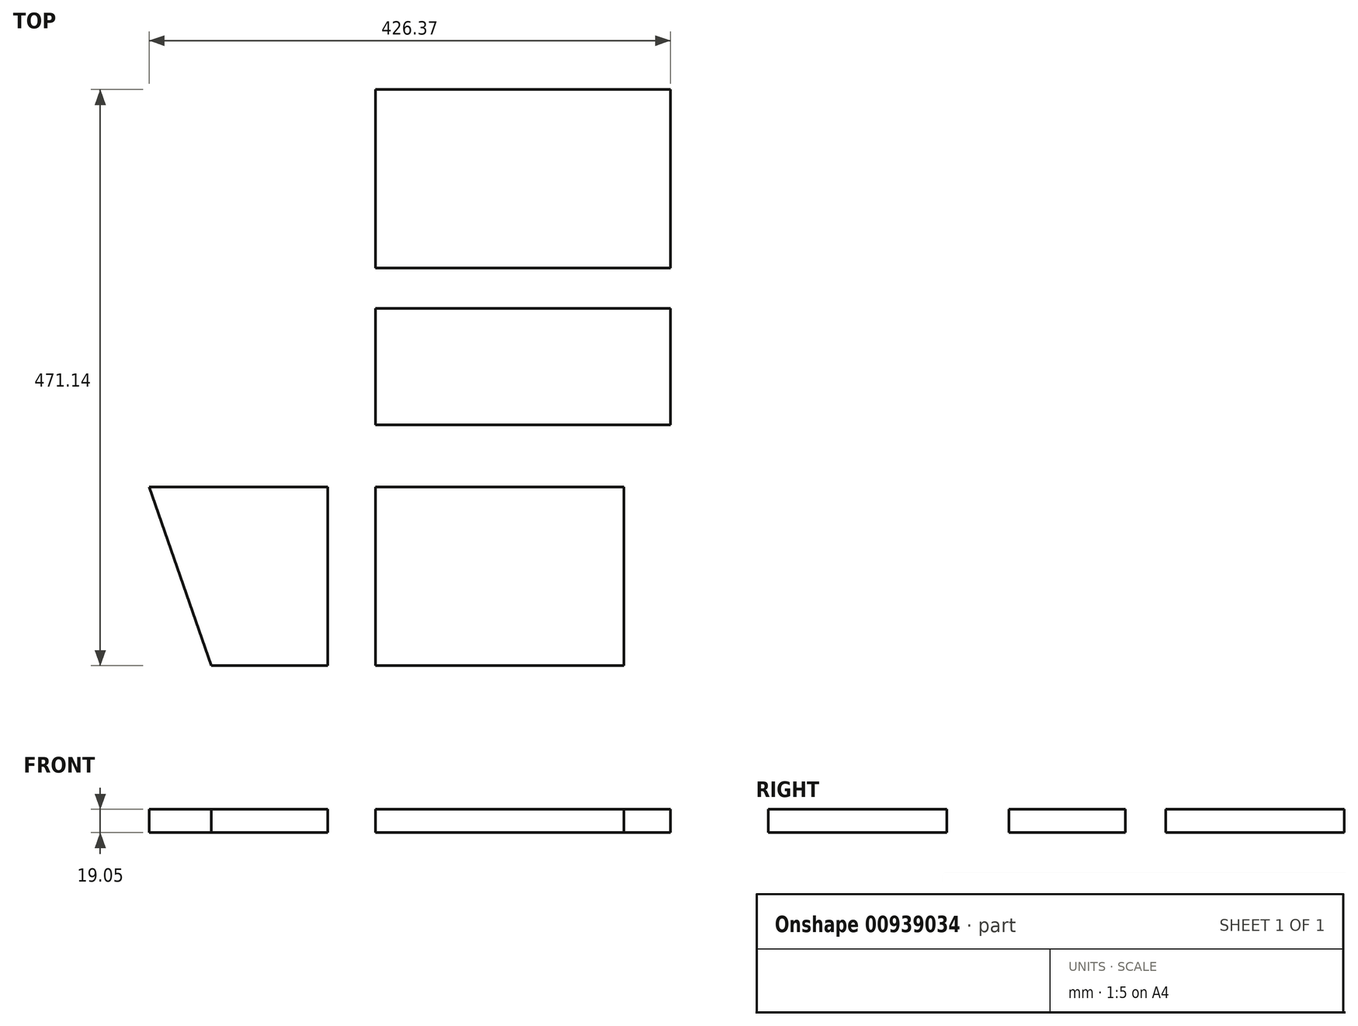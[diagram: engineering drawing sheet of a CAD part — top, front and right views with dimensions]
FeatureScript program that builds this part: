
annotation { "Feature Type Name" : "Feature", "Feature Type Description" : "" }
export const myFeature = defineFeature(function(context is Context, id is Id, definition is map)
    precondition{}
    {
        {
            var Q0;
            Q0=qCreatedBy(makeId("Front.planeOp"),FACE);
            var sketch = newSketch(context, id + "F0", { "sketchPlane" : qUnion([Q0])});
            skLineSegment(sketch, "E0.bottom", {"start": v(0, 0) * mm, "end": v(203.2, 0) * mm});
            skLineSegment(sketch, "E0.top", {"start": v(0, 19.05) * mm, "end": v(203.2, 19.05) * mm});
            skLineSegment(sketch, "E0.left", {"start": v(0, 0) * mm, "end": v(0, 19.05) * mm});
            skLineSegment(sketch, "E0.right", {"start": v(203.2, 0) * mm, "end": v(203.2, 19.05) * mm});
            skSolve(sketch);
        }
        {
            var Q0;
            Q0 = qSketchRegion(id + "F0", true);
            extrude(context, id + "F1", {"entities" : qUnion([Q0]), "depth" : 146.05 * mm, "offsetDistance" : 25.4 * mm});
        }
        {
            var Q0;
            Q0=qCreatedBy(makeId("Top.planeOp"),FACE);
            var sketch = newSketch(context, id + "F2", { "sketchPlane" : qUnion([Q0])});
            skLineSegment(sketch, "E1.bottom", {"start": v(0, 50.8) * mm, "end": v(241.3, 50.8) * mm});
            skLineSegment(sketch, "E1.top", {"start": v(0, 146.05) * mm, "end": v(241.3, 146.05) * mm});
            skLineSegment(sketch, "E1.left", {"start": v(0, 50.8) * mm, "end": v(0, 146.05) * mm});
            skLineSegment(sketch, "E1.right", {"start": v(241.3, 50.8) * mm, "end": v(241.3, 146.05) * mm});
            skSolve(sketch);
        }
        {
            var Q0;
            Q0 = qSketchRegion(id + "F2", true);
            extrude(context, id + "F3", {"entities" : qUnion([Q0]), "depth" : 19.05 * mm, "offsetDistance" : 25.4 * mm});
        }
        {
            var Q0;
            Q0=qCreatedBy(makeId("Top.planeOp"),FACE);
            var sketch = newSketch(context, id + "F4", { "sketchPlane" : qUnion([Q0])});
            skLineSegment(sketch, "E2.bottom", {"start": v(0, 179.04) * mm, "end": v(241.3, 179.04) * mm});
            skLineSegment(sketch, "E2.top", {"start": v(0, 325.09) * mm, "end": v(241.3, 325.09) * mm});
            skLineSegment(sketch, "E2.left", {"start": v(0, 179.04) * mm, "end": v(0, 325.09) * mm});
            skLineSegment(sketch, "E2.right", {"start": v(241.3, 179.04) * mm, "end": v(241.3, 325.09) * mm});
            skSolve(sketch);
        }
        {
            var Q0;
            Q0 = qSketchRegion(id + "F4", true);
            extrude(context, id + "F5", {"entities" : qUnion([Q0]), "depth" : 19.05 * mm, "offsetDistance" : 25.4 * mm});
        }
        {
            var Q0;
            Q0=qCreatedBy(makeId("Top.planeOp"),FACE);
            var sketch = newSketch(context, id + "F6", { "sketchPlane" : qUnion([Q0])});
            skLineSegment(sketch, "E3.bottom", {"start": v(-39.02, 0) * mm, "end": v(-185.07, 0) * mm});
            skLineSegment(sketch, "E3.top", {"start": v(-39.02, -146.05) * mm, "end": v(-185.07, -146.05) * mm});
            skLineSegment(sketch, "E3.left", {"start": v(-39.02, 0) * mm, "end": v(-39.02, -146.05) * mm});
            skLineSegment(sketch, "E3.right", {"start": v(-185.07, 0) * mm, "end": v(-185.07, -146.05) * mm});
            skSolve(sketch);
        }
        {
            var Q0;
            Q0 = qSketchRegion(id + "F6", true);
            extrude(context, id + "F7", {"entities" : qUnion([Q0]), "depth" : 19.05 * mm, "offsetDistance" : 25.4 * mm});
        }
        {
            var Q0;
            Q0=makeQuery(id+"F7.opExtrude","CAP_FACE",FACE,{"disambiguationData":[OSD([sQuery(id+"F6.wireOp",EDGE,"E3.bottom"),sQuery(id+"F6.wireOp",EDGE,"E3.top"),sQuery(id+"F6.wireOp",EDGE,"E3.left"),sQuery(id+"F6.wireOp",EDGE,"E3.right")])],"isStart":false});
            var sketch = newSketch(context, id + "F8", { "sketchPlane" : qUnion([Q0])});
            skLineSegment(sketch, "E4", {"start": v(-185.07, 0) * mm, "end": v(-185.07, -146.05) * mm});
            skLineSegment(sketch, "E5", {"start": v(-185.07, -146.05) * mm, "end": v(-134.27, -146.05) * mm});
            skLineSegment(sketch, "E6", {"start": v(-134.27, -146.05) * mm, "end": v(-185.07, 0) * mm});
            skSolve(sketch);
        }
        {
            var Q0;
            Q0 = qSketchRegion(id + "F8", true);
            extrude(context, id + "F9", {"entities" : qUnion([Q0]), "operationType" : NewBodyOperationType.REMOVE, "endBound" : BoundingType.THROUGH_ALL, "oppositeDirection" : true, "depth" : 25.4 * mm, "offsetDistance" : 25.4 * mm});
        }
    });
